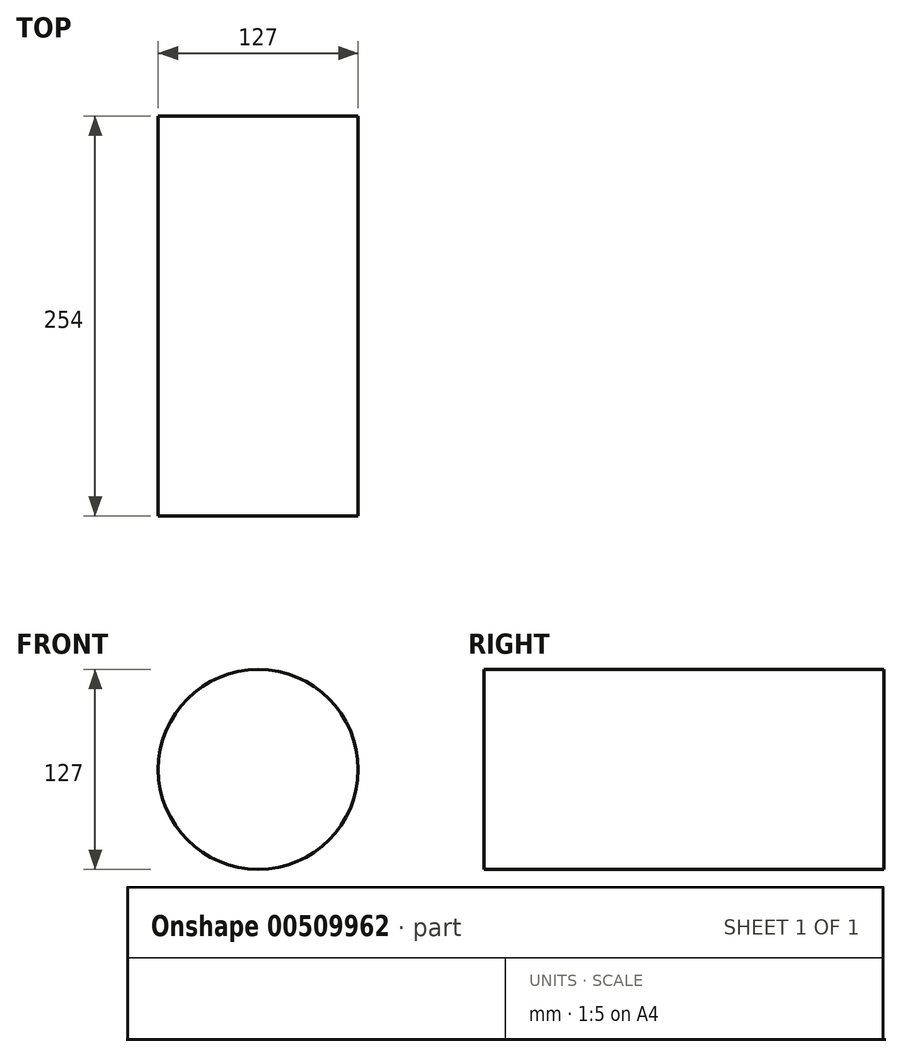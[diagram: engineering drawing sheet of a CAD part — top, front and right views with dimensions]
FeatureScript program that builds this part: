
annotation { "Feature Type Name" : "Feature", "Feature Type Description" : "" }
export const myFeature = defineFeature(function(context is Context, id is Id, definition is map)
    precondition{}
    {
        {
            var Q0;
            Q0=qCreatedBy(makeId("Front.planeOp"),FACE);
            var sketch = newSketch(context, id + "F0", { "sketchPlane" : qUnion([Q0])});
            skCircle(sketch, "E0", {"center": v(0, 12.29) * mm, "radius": 63.5 * mm});
            skSolve(sketch);
        }
        {
            var Q0;
            Q0 = qSketchRegion(id + "F0", true);
            extrude(context, id + "F1", {"entities" : qUnion([Q0]), "depth" : 254 * mm});
        }
    });
